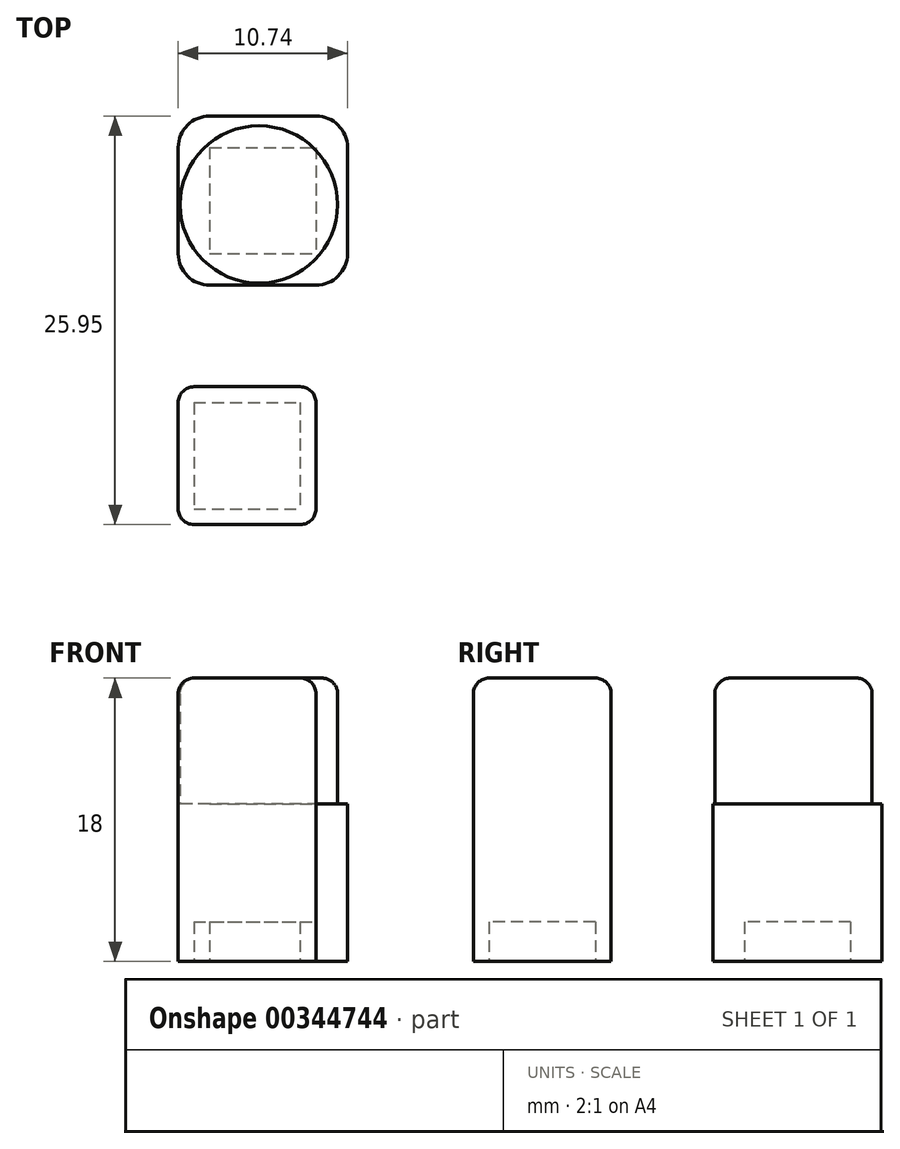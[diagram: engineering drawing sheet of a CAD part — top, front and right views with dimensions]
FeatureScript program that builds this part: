
annotation { "Feature Type Name" : "Feature", "Feature Type Description" : "" }
export const myFeature = defineFeature(function(context is Context, id is Id, definition is map)
    precondition{}
    {
        {
            var Q0;
            Q0=qCreatedBy(makeId("Top.planeOp"),FACE);
            var sketch = newSketch(context, id + "F0", { "sketchPlane" : qUnion([Q0])});
            skLineSegment(sketch, "E0.bottom", {"start": v(-3.12, 3.62) * mm, "end": v(3.62, 3.62) * mm});
            skLineSegment(sketch, "E0.top", {"start": v(-3.12, -3.13) * mm, "end": v(3.62, -3.12) * mm});
            skLineSegment(sketch, "E0.left", {"start": v(-3.12, 3.62) * mm, "end": v(-3.12, -3.13) * mm});
            skLineSegment(sketch, "E0.right", {"start": v(3.62, 3.63) * mm, "end": v(3.62, -3.12) * mm});
            skLineSegment(sketch, "E1.0", {"start": v(-5.12, 5.62) * mm, "end": v(5.62, 5.63) * mm});
            skLineSegment(sketch, "E1.1", {"start": v(-5.12, 5.62) * mm, "end": v(-5.12, -5.13) * mm});
            skLineSegment(sketch, "E1.2", {"start": v(-5.13, -5.13) * mm, "end": v(5.62, -5.12) * mm});
            skLineSegment(sketch, "E1.3", {"start": v(5.62, 5.63) * mm, "end": v(5.62, -5.12) * mm});
            skSolve(sketch);
        }
        {
            var Q0;
            Q0=makeQuery(id+"F0.imprint","IMPRINT",FACE,{"disambiguationData":[TD([[makeQuery(id+"F0.imprint","IMPRINT",EDGE,{"derivedFrom":sQuery(id+"F0.wireOp",EDGE,"E0.bottom")}),1.0]])]});
            var Q1;
            Q1=makeQuery(id+"F0.imprint","IMPRINT",FACE,{"disambiguationData":[TD([[makeQuery(id+"F0.imprint","IMPRINT",EDGE,{"derivedFrom":sQuery(id+"F0.wireOp",EDGE,"E0.bottom")}),-1.0]])]});
            extrude(context, id + "F1", {"entities" : qUnion([Q0, Q1]), "depth" : 10 * mm});
        }
        {
            var Q0;
            Q0=makeQuery(id+"F0.imprint","IMPRINT",FACE,{"disambiguationData":[TD([[makeQuery(id+"F0.imprint","IMPRINT",EDGE,{"derivedFrom":sQuery(id+"F0.wireOp",EDGE,"E0.bottom")}),-1.0]])]});
            extrude(context, id + "F2", {"entities" : qUnion([Q0]), "operationType" : NewBodyOperationType.REMOVE, "depth" : 2.5 * mm});
        }
        {
            var Q0;
            Q0=makeQuery(id+"F1.opExtrude","CAP_FACE",FACE,{"disambiguationData":[OSD([sQuery(id+"F0.wireOp",EDGE,"E1.0"),sQuery(id+"F0.wireOp",EDGE,"E1.1"),sQuery(id+"F0.wireOp",EDGE,"E1.2"),sQuery(id+"F0.wireOp",EDGE,"E1.3")])],"isStart":false});
            var sketch = newSketch(context, id + "F3", { "sketchPlane" : qUnion([Q0])});
            skCircle(sketch, "E2", {"center": v(0, 0) * mm, "radius": 5 * mm});
            skSolve(sketch);
        }
        {
            var Q0;
            Q0=makeQuery(id+"F3.imprint","IMPRINT",FACE,{"disambiguationData":[TD([[makeQuery(id+"F3.imprint","IMPRINT",EDGE,{"derivedFrom":sQuery(id+"F3.wireOp",EDGE,"E2")}),1.0]])]});
            extrude(context, id + "F4", {"entities" : qUnion([Q0]), "operationType" : NewBodyOperationType.ADD, "depth" : 8 * mm});
        }
        {
            var Q0;
            Q0=makeQuery(id+"F1.opExtrude","SWEPT_EDGE",EDGE,{"disambiguationData":[OSD([sQuery(id+"F0.wireOp",EDGE,"E1.1"),sQuery(id+"F0.wireOp",EDGE,"E1.2")])]});
            var Q1;
            Q1=makeQuery(id+"F1.opExtrude","SWEPT_EDGE",EDGE,{"disambiguationData":[OSD([sQuery(id+"F0.wireOp",EDGE,"E1.2"),sQuery(id+"F0.wireOp",EDGE,"E1.3")])]});
            var Q2;
            Q2=makeQuery(id+"F1.opExtrude","SWEPT_EDGE",EDGE,{"disambiguationData":[OSD([sQuery(id+"F0.wireOp",EDGE,"E1.0"),sQuery(id+"F0.wireOp",EDGE,"E1.3")])]});
            var Q3;
            Q3=makeQuery(id+"F1.opExtrude","SWEPT_EDGE",EDGE,{"disambiguationData":[OSD([sQuery(id+"F0.wireOp",EDGE,"E1.0"),sQuery(id+"F0.wireOp",EDGE,"E1.1")])]});
            fillet(context, id + "F5", {"entities" : qUnion([Q0, Q1, Q2, Q3]), "radius" : 2 * mm, "tangentPropagation" : true, "allowEdgeOverflow" : false});
        }
        {
            var Q0;
            Q0=makeQuery(id+"F4.opExtrude","CAP_EDGE",EDGE,{"disambiguationData":[OSD([sQuery(id+"F3.wireOp",EDGE,"E2")])],"isStart":false});
            fillet(context, id + "F6", {"entities" : qUnion([Q0]), "radius" : 1 * mm, "tangentPropagation" : true, "allowEdgeOverflow" : false});
        }
        {
            var Q0;
            Q0=qCreatedBy(makeId("Top.planeOp"),FACE);
            var sketch = newSketch(context, id + "F7", { "sketchPlane" : qUnion([Q0])});
            skLineSegment(sketch, "E3.bottom", {"start": v(-4.12, -12.58) * mm, "end": v(2.62, -12.58) * mm});
            skLineSegment(sketch, "E3.top", {"start": v(-4.12, -19.33) * mm, "end": v(2.62, -19.33) * mm});
            skLineSegment(sketch, "E3.left", {"start": v(-4.12, -12.58) * mm, "end": v(-4.12, -19.33) * mm});
            skLineSegment(sketch, "E3.right", {"start": v(2.62, -12.58) * mm, "end": v(2.62, -19.33) * mm});
            skLineSegment(sketch, "E4.0", {"start": v(-5.12, -11.58) * mm, "end": v(3.62, -11.58) * mm});
            skLineSegment(sketch, "E4.1", {"start": v(-5.12, -11.58) * mm, "end": v(-5.12, -20.33) * mm});
            skLineSegment(sketch, "E4.2", {"start": v(-5.12, -20.33) * mm, "end": v(3.62, -20.33) * mm});
            skLineSegment(sketch, "E4.3", {"start": v(3.62, -11.58) * mm, "end": v(3.62, -20.33) * mm});
            skSolve(sketch);
        }
        {
            var Q0;
            Q0=makeQuery(id+"F7.imprint","IMPRINT",FACE,{"disambiguationData":[TD([[makeQuery(id+"F7.imprint","IMPRINT",EDGE,{"derivedFrom":sQuery(id+"F7.wireOp",EDGE,"E3.bottom")}),1.0]])]});
            var Q1;
            Q1=makeQuery(id+"F7.imprint","IMPRINT",FACE,{"disambiguationData":[TD([[makeQuery(id+"F7.imprint","IMPRINT",EDGE,{"derivedFrom":sQuery(id+"F7.wireOp",EDGE,"E3.bottom")}),-1.0]])]});
            extrude(context, id + "F8", {"entities" : qUnion([Q0, Q1]), "depth" : 18 * mm});
        }
        {
            var Q0;
            Q0=makeQuery(id+"F7.imprint","IMPRINT",FACE,{"disambiguationData":[TD([[makeQuery(id+"F7.imprint","IMPRINT",EDGE,{"derivedFrom":sQuery(id+"F7.wireOp",EDGE,"E3.bottom")}),-1.0]])]});
            extrude(context, id + "F9", {"entities" : qUnion([Q0]), "operationType" : NewBodyOperationType.REMOVE, "depth" : 2.5 * mm});
        }
        {
            var Q0;
            Q0=makeQuery(id+"F8.opExtrude","SWEPT_EDGE",EDGE,{"disambiguationData":[OSD([sQuery(id+"F7.wireOp",EDGE,"E4.0"),sQuery(id+"F7.wireOp",EDGE,"E4.1")])]});
            var Q1;
            Q1=makeQuery(id+"F8.opExtrude","SWEPT_EDGE",EDGE,{"disambiguationData":[OSD([sQuery(id+"F7.wireOp",EDGE,"E4.0"),sQuery(id+"F7.wireOp",EDGE,"E4.3")])]});
            var Q2;
            Q2=makeQuery(id+"F8.opExtrude","SWEPT_EDGE",EDGE,{"disambiguationData":[OSD([sQuery(id+"F7.wireOp",EDGE,"E4.1"),sQuery(id+"F7.wireOp",EDGE,"E4.2")])]});
            var Q3;
            Q3=makeQuery(id+"F8.opExtrude","SWEPT_EDGE",EDGE,{"disambiguationData":[OSD([sQuery(id+"F7.wireOp",EDGE,"E4.2"),sQuery(id+"F7.wireOp",EDGE,"E4.3")])]});
            var Q4;
            Q4=makeQuery(id+"F8.opExtrude","CAP_FACE",FACE,{"disambiguationData":[OSD([sQuery(id+"F7.wireOp",EDGE,"E4.0"),sQuery(id+"F7.wireOp",EDGE,"E4.1"),sQuery(id+"F7.wireOp",EDGE,"E4.2"),sQuery(id+"F7.wireOp",EDGE,"E4.3")])],"isStart":false});
            fillet(context, id + "F10", {"entities" : qUnion([Q0, Q1, Q2, Q3, Q4]), "radius" : 1 * mm, "tangentPropagation" : true, "allowEdgeOverflow" : false});
        }
    });
